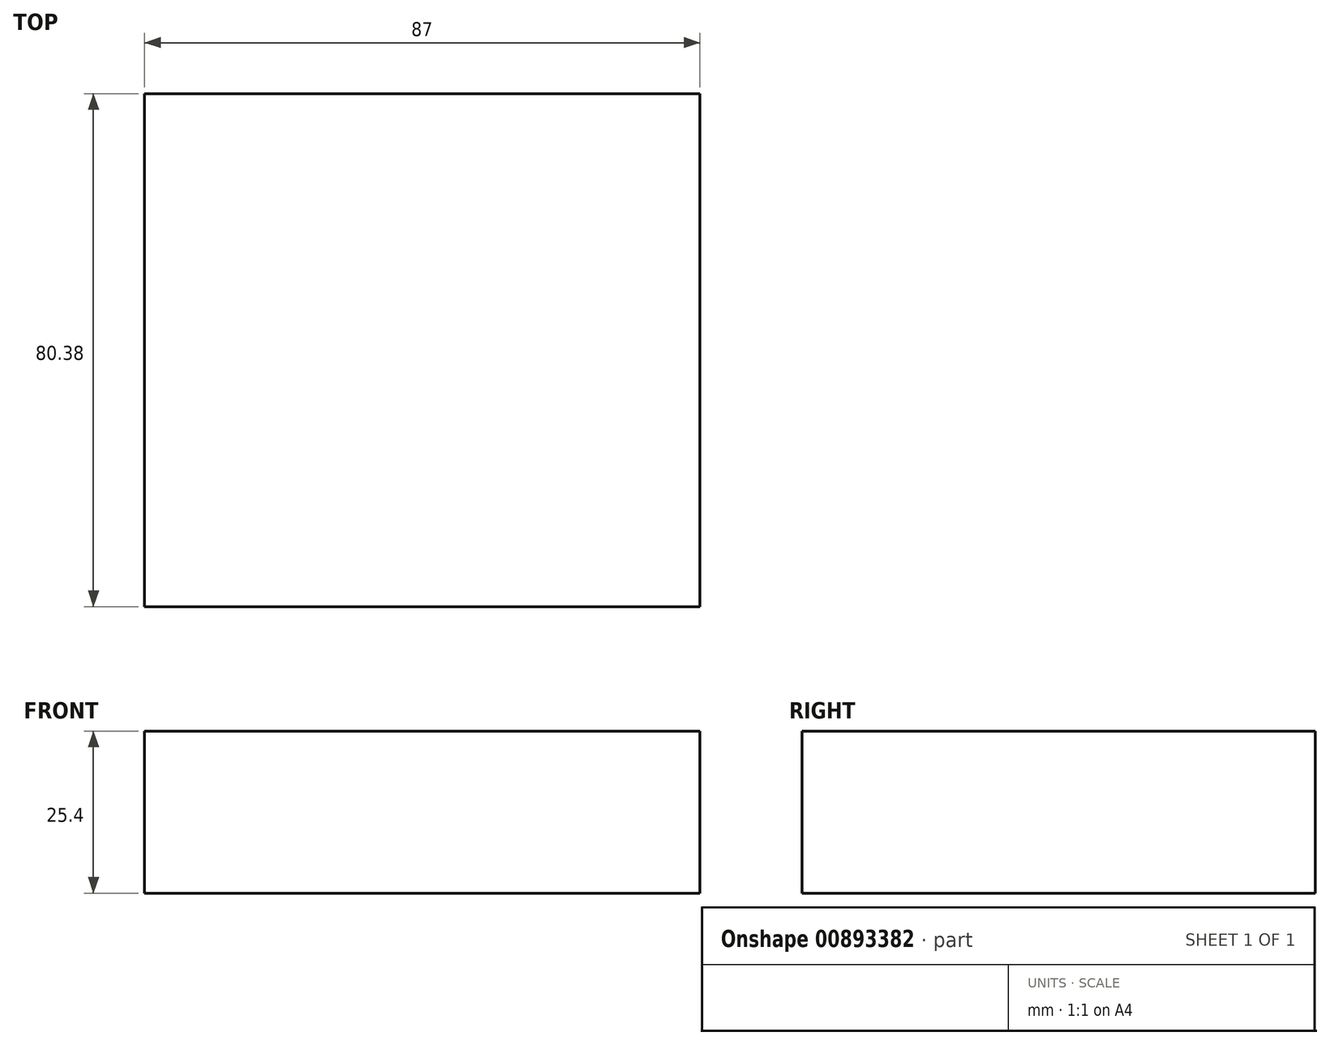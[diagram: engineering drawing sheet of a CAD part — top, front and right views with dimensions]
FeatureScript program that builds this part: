
annotation { "Feature Type Name" : "Feature", "Feature Type Description" : "" }
export const myFeature = defineFeature(function(context is Context, id is Id, definition is map)
    precondition{}
    {
        {
            var Q0;
            Q0=qCreatedBy(makeId("Top.planeOp"),FACE);
            var sketch = newSketch(context, id + "F0", { "sketchPlane" : qUnion([Q0])});
            skLineSegment(sketch, "E0.bottom", {"start": v(-43.04, 32.46) * mm, "end": v(43.96, 32.46) * mm});
            skLineSegment(sketch, "E0.top", {"start": v(-43.04, -47.92) * mm, "end": v(43.96, -47.92) * mm});
            skLineSegment(sketch, "E0.left", {"start": v(-43.04, 32.46) * mm, "end": v(-43.04, -47.92) * mm});
            skLineSegment(sketch, "E0.right", {"start": v(43.96, 32.46) * mm, "end": v(43.96, -47.92) * mm});
            skSolve(sketch);
        }
        {
            var Q0;
            Q0 = qSketchRegion(id + "F0", true);
            extrude(context, id + "F1", {"entities" : qUnion([Q0]), "depth" : 25.4 * mm, "offsetDistance" : 25.4 * mm});
        }
    });
